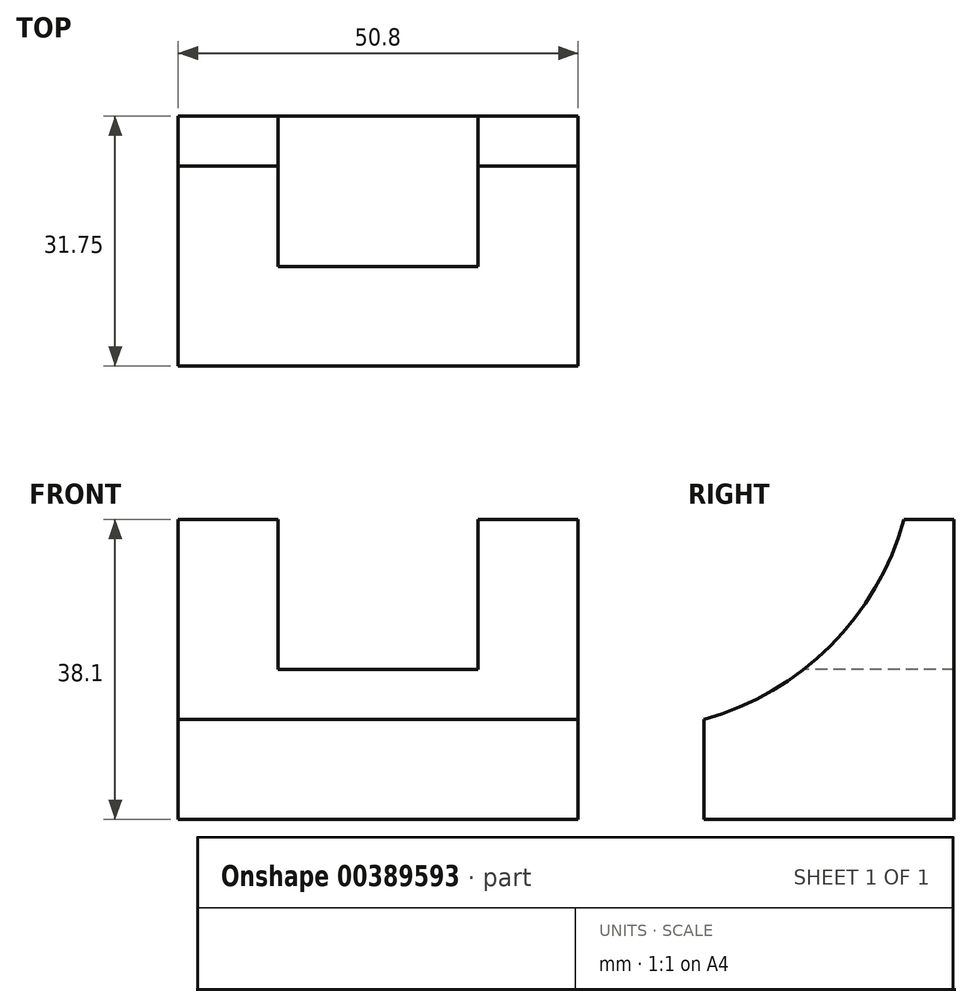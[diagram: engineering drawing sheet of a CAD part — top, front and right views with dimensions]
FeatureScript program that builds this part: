
annotation { "Feature Type Name" : "Feature", "Feature Type Description" : "" }
export const myFeature = defineFeature(function(context is Context, id is Id, definition is map)
    precondition{}
    {
        {
            var Q0;
            Q0=qCreatedBy(makeId("Front.planeOp"),FACE);
            var sketch = newSketch(context, id + "F0", { "sketchPlane" : qUnion([Q0])});
            skLineSegment(sketch, "E0.bottom", {"start": v(0, 38.1) * mm, "end": v(50.8, 38.1) * mm});
            skLineSegment(sketch, "E0.top", {"start": v(0, 0) * mm, "end": v(50.8, 0) * mm});
            skLineSegment(sketch, "E0.left", {"start": v(0, 38.1) * mm, "end": v(0, 0) * mm});
            skLineSegment(sketch, "E0.right", {"start": v(50.8, 38.1) * mm, "end": v(50.8, 0) * mm});
            skSolve(sketch);
        }
        {
            var Q0;
            Q0=makeQuery(id+"F0.imprint","IMPRINT",FACE,{"disambiguationData":[TD([[makeQuery(id+"F0.imprint","IMPRINT",EDGE,{"derivedFrom":sQuery(id+"F0.wireOp",EDGE,"E0.bottom")}),-1.0]])]});
            extrude(context, id + "F1", {"entities" : qUnion([Q0]), "depth" : 31.75 * mm});
        }
        {
            var Q0;
            Q0=makeQuery(id+"F1.opExtrude","CAP_FACE",FACE,{"disambiguationData":[OSD([sQuery(id+"F0.wireOp",EDGE,"E0.bottom"),sQuery(id+"F0.wireOp",EDGE,"E0.top"),sQuery(id+"F0.wireOp",EDGE,"E0.left"),sQuery(id+"F0.wireOp",EDGE,"E0.right")])],"isStart":false});
            var sketch = newSketch(context, id + "F2", { "sketchPlane" : qUnion([Q0])});
            skLineSegment(sketch, "E1", {"start": v(12.7, 38.1) * mm, "end": v(12.7, 19.05) * mm});
            skLineSegment(sketch, "E2", {"start": v(12.7, 19.05) * mm, "end": v(38.1, 19.05) * mm});
            skLineSegment(sketch, "E3", {"start": v(38.1, 19.05) * mm, "end": v(38.1, 38.1) * mm});
            skLineSegment(sketch, "E4", {"start": v(38.1, 38.1) * mm, "end": v(12.7, 38.1) * mm});
            skSolve(sketch);
        }
        {
            var Q0;
            Q0=makeQuery(id+"F2.imprint","IMPRINT",FACE,{"disambiguationData":[TD([[makeQuery(id+"F2.imprint","IMPRINT",EDGE,{"derivedFrom":sQuery(id+"F2.wireOp",EDGE,"E1")}),1.0]])]});
            extrude(context, id + "F3", {"entities" : qUnion([Q0]), "operationType" : NewBodyOperationType.REMOVE, "oppositeDirection" : true, "depth" : 38.1 * mm});
        }
        {
            var Q0;
            Q0=makeQuery(id+"F1.opExtrude","SWEPT_FACE",FACE,{"disambiguationData":[OSD([sQuery(id+"F0.wireOp",EDGE,"E0.right")])]});
            var sketch = newSketch(context, id + "F4", { "sketchPlane" : qUnion([Q0])});
            skLineSegment(sketch, "E5.bottom", {"start": v(-31.75, 38.1) * mm, "end": v(0, 38.1) * mm});
            skLineSegment(sketch, "E5.top", {"start": v(-31.75, 0) * mm, "end": v(0, 0) * mm});
            skLineSegment(sketch, "E5.left", {"start": v(-31.75, 38.1) * mm, "end": v(-31.75, 0) * mm});
            skLineSegment(sketch, "E5.right", {"start": v(0, 38.1) * mm, "end": v(0, 0) * mm});
            skArc(sketch, "E6", {"start": v(-31.75, 12.7) * mm, "mid": v(-15.7, 22.05) * mm, "end": v(-6.35, 38.1) * mm});
            skSolve(sketch);
        }
        {
            var Q0;
            {var subQ3=sQuery(id+"F4.wireOp",EDGE,"E6");Q0=makeQuery(id+"F4.imprint","IMPRINT",FACE,{"disambiguationData":[TD([[makeQuery(id+"F4.imprint","IMPRINT",EDGE,{"derivedFrom":subQ3}),1.0]])]});}
            extrude(context, id + "F5", {"entities" : qUnion([Q0]), "operationType" : NewBodyOperationType.REMOVE, "oppositeDirection" : true, "depth" : 76.2 * mm});
        }
    });
